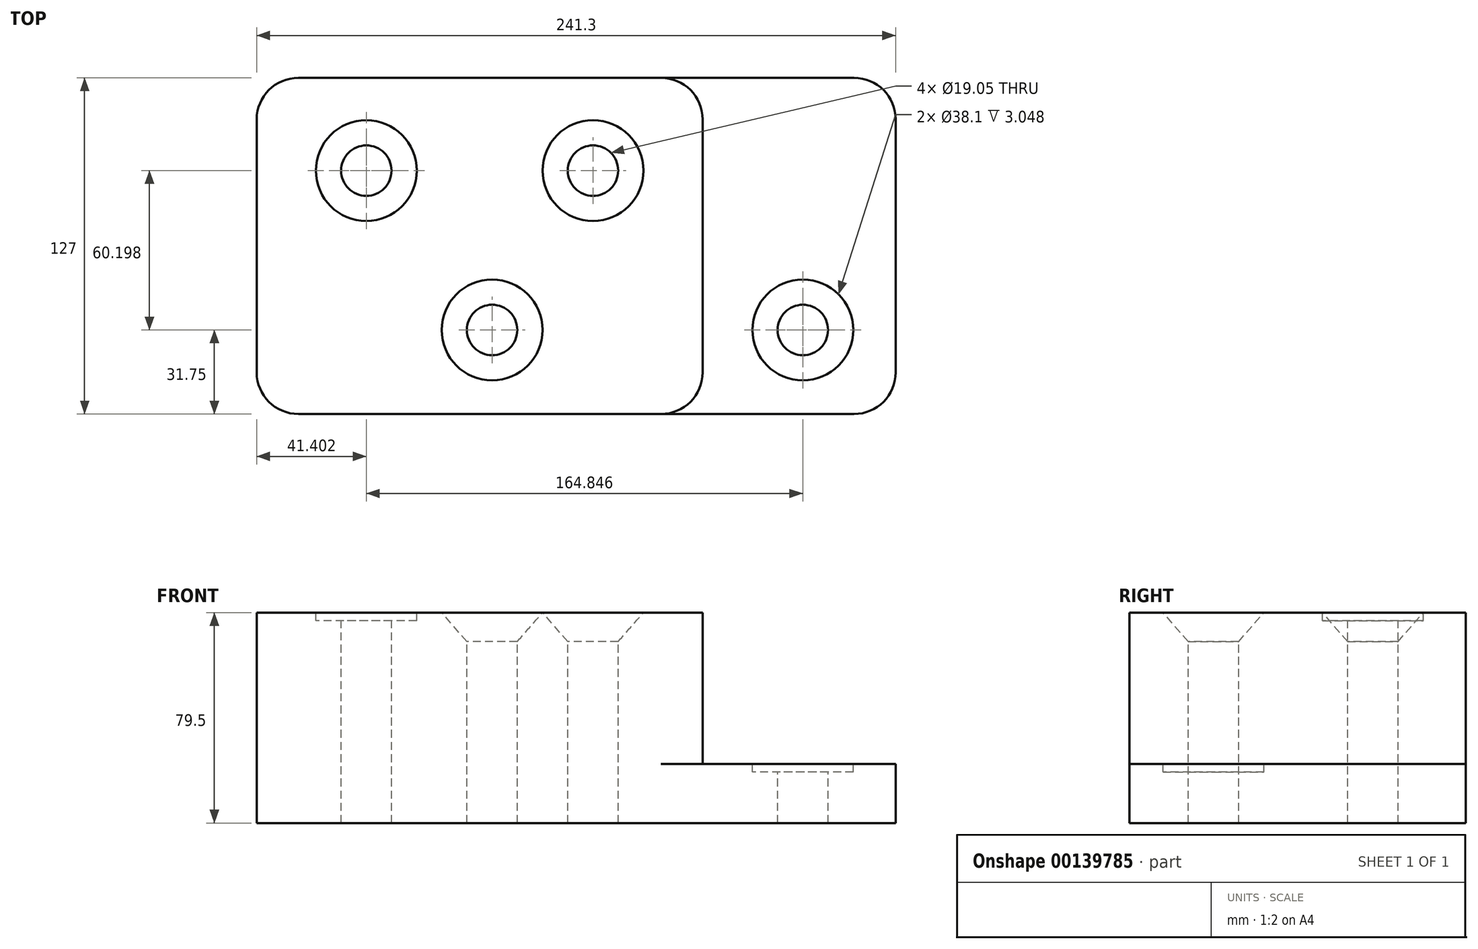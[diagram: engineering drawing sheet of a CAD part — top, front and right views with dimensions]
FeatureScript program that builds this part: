
annotation { "Feature Type Name" : "Feature", "Feature Type Description" : "" }
export const myFeature = defineFeature(function(context is Context, id is Id, definition is map)
    precondition{}
    {
        {
            var Q0;
            Q0=qCreatedBy(makeId("Front.planeOp"),FACE);
            var sketch = newSketch(context, id + "F0", { "sketchPlane" : qUnion([Q0])});
            skLineSegment(sketch, "E0", {"start": v(0, 0) * mm, "end": v(0, 79.5) * mm});
            skLineSegment(sketch, "E1", {"start": v(0, 79.5) * mm, "end": v(168.4, 79.5) * mm});
            skLineSegment(sketch, "E2", {"start": v(168.4, 79.5) * mm, "end": v(168.4, 22.35) * mm});
            skLineSegment(sketch, "E3", {"start": v(168.4, 22.35) * mm, "end": v(241.3, 22.35) * mm});
            skLineSegment(sketch, "E4", {"start": v(241.3, 22.35) * mm, "end": v(241.3, 0) * mm});
            skLineSegment(sketch, "E5", {"start": v(241.3, 0) * mm, "end": v(0, 0) * mm});
            skSolve(sketch);
        }
        {
            var Q0;
            Q0 = qSketchRegion(id + "F0", true);
            extrude(context, id + "F1", {"entities" : qUnion([Q0]), "depth" : 127 * mm});
        }
        {
            var Q0;
            Q0=makeQuery(id+"F1.opExtrude","SWEPT_FACE",FACE,{"disambiguationData":[OSD([sQuery(id+"F0.wireOp",EDGE,"E1")])]});
            cPlane(context, id + "F2", {"entities" : qUnion([Q0]), "cplaneType" : CPlaneType.OFFSET, "offset" : 25.4 * mm, "width" : 152.4 * mm, "height" : 152.4 * mm});
        }
        {
            var Q0;
            Q0=qCreatedBy(id+"F2.planeOp",FACE);
            var sketch = newSketch(context, id + "F3", { "sketchPlane" : qUnion([Q0])});
            skPoint(sketch, "E6", {"position": v(88.9, -95.25) * mm});
            skPoint(sketch, "E7", {"position": v(127, -35.05) * mm});
            skPoint(sketch, "E8", {"position": v(41.4, -35.05) * mm});
            skPoint(sketch, "E9", {"position": v(206.25, -95.25) * mm});
            skSolve(sketch);
        }
        {
            var Q0;
            Q0=sQuery(id+"F3.wireOp",VERTEX,"E7");
            var Q1;
            Q1=sQuery(id+"F3.wireOp",VERTEX,"E6");
            var Q2;
            Q2=makeQuery(id+"F1.opExtrude","SWEPT_BODY",BODY,{"disambiguationData":[OSD([sQuery(id+"F0.wireOp",EDGE,"E0"),sQuery(id+"F0.wireOp",EDGE,"E1"),sQuery(id+"F0.wireOp",EDGE,"E2"),sQuery(id+"F0.wireOp",EDGE,"E3"),sQuery(id+"F0.wireOp",EDGE,"E4"),sQuery(id+"F0.wireOp",EDGE,"E5")])]});
            hole(context, id + "F4", {"style" : HoleStyle.C_SINK, "endStyle" : HoleEndStyle.THROUGH, "holeDiameter" : 19.05 * mm, "cSinkDiameter" : 38.1 * mm, "cSinkAngle" : 82 * degree, "locations" : qUnion([Q0, Q1]), "scope" : qUnion([Q2]), "isTappedThrough" : true});
        }
        {
            var Q0;
            Q0=sQuery(id+"F3.wireOp",VERTEX,"E8");
            var Q1;
            Q1=sQuery(id+"F3.wireOp",VERTEX,"E9");
            var Q2;
            Q2=makeQuery(id+"F1.opExtrude","SWEPT_BODY",BODY,{"disambiguationData":[OSD([sQuery(id+"F0.wireOp",EDGE,"E0"),sQuery(id+"F0.wireOp",EDGE,"E1"),sQuery(id+"F0.wireOp",EDGE,"E2"),sQuery(id+"F0.wireOp",EDGE,"E3"),sQuery(id+"F0.wireOp",EDGE,"E4"),sQuery(id+"F0.wireOp",EDGE,"E5")])]});
            hole(context, id + "F5", {"style" : HoleStyle.C_BORE, "endStyle" : HoleEndStyle.THROUGH, "holeDiameter" : 19.05 * mm, "cBoreDiameter" : 38.1 * mm, "cBoreDepth" : 3.05 * mm, "locations" : qUnion([Q0, Q1]), "scope" : qUnion([Q2]), "isTappedThrough" : true});
        }
        {
            var Q0;
            Q0=makeQuery(id+"F1.opExtrude","CAP_EDGE",EDGE,{"disambiguationData":[OSD([sQuery(id+"F0.wireOp",EDGE,"E4")])],"isStart":false});
            var Q1;
            Q1=makeQuery(id+"F1.opExtrude","CAP_EDGE",EDGE,{"disambiguationData":[OSD([sQuery(id+"F0.wireOp",EDGE,"E4")])],"isStart":true});
            var Q2;
            Q2=makeQuery(id+"F1.opExtrude","CAP_EDGE",EDGE,{"disambiguationData":[OSD([sQuery(id+"F0.wireOp",EDGE,"E2")])],"isStart":true});
            var Q3;
            Q3=makeQuery(id+"F1.opExtrude","CAP_EDGE",EDGE,{"disambiguationData":[OSD([sQuery(id+"F0.wireOp",EDGE,"E2")])],"isStart":false});
            var Q4;
            Q4=makeQuery(id+"F1.opExtrude","CAP_EDGE",EDGE,{"disambiguationData":[OSD([sQuery(id+"F0.wireOp",EDGE,"E0")])],"isStart":false});
            var Q5;
            Q5=makeQuery(id+"F1.opExtrude","CAP_EDGE",EDGE,{"disambiguationData":[OSD([sQuery(id+"F0.wireOp",EDGE,"E0")])],"isStart":true});
            fillet(context, id + "F6", {"entities" : qUnion([Q0, Q1, Q2, Q3, Q4, Q5]), "radius" : 15.75 * mm, "tangentPropagation" : true, "allowEdgeOverflow" : false});
        }
    });
